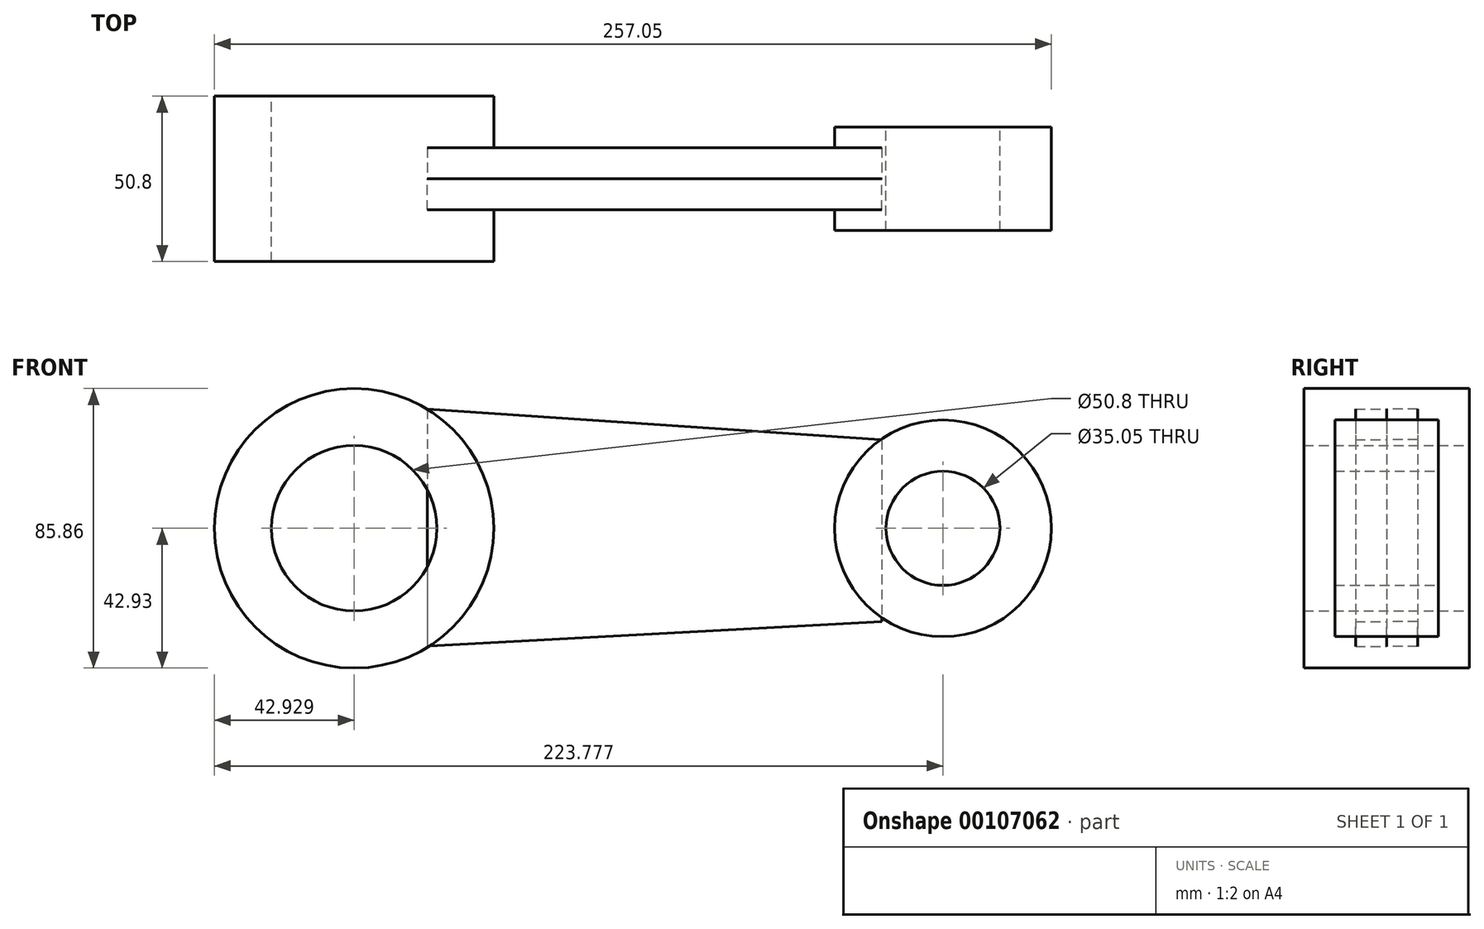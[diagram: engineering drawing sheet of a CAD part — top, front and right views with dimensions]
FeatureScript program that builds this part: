
annotation { "Feature Type Name" : "Feature", "Feature Type Description" : "" }
export const myFeature = defineFeature(function(context is Context, id is Id, definition is map)
    precondition{}
    {
        {
            var Q0;
            Q0=qCreatedBy(makeId("Front.planeOp"),FACE);
            var sketch = newSketch(context, id + "F0", { "sketchPlane" : qUnion([Q0])});
            skLineSegment(sketch, "E0", {"start": v(-64.98, 0) * mm, "end": v(115.87, 0) * mm});
            skCircle(sketch, "E1", {"center": v(-64.98, 0) * mm, "radius": 25.4 * mm});
            skCircle(sketch, "E2", {"center": v(-64.98, 0) * mm, "radius": 42.93 * mm});
            skCircle(sketch, "E3", {"center": v(115.87, 0) * mm, "radius": 17.53 * mm});
            skCircle(sketch, "E4", {"center": v(115.87, 0) * mm, "radius": 33.27 * mm});
            skSolve(sketch);
        }
        {
            var Q0;
            Q0=makeQuery(id+"F0.imprint","IMPRINT",FACE,{"disambiguationData":[TD([[makeQuery(id+"F0.imprint","IMPRINT",EDGE,{"derivedFrom":sQuery(id+"F0.wireOp",EDGE,"E3")}),-1.0]])]});
            extrude(context, id + "F1", {"entities" : qUnion([Q0]), "depth" : 15.88 * mm});
        }
        {
            var Q0;
            Q0=makeQuery(id+"F0.imprint","IMPRINT",FACE,{"disambiguationData":[TD([[makeQuery(id+"F0.imprint","IMPRINT",EDGE,{"derivedFrom":sQuery(id+"F0.wireOp",EDGE,"E1")}),-1.0]])]});
            extrude(context, id + "F2", {"entities" : qUnion([Q0]), "depth" : 25.4 * mm});
        }
        {
            var Q0;
            Q0=makeQuery(id+"F0.imprint","IMPRINT",FACE,{"disambiguationData":[TD([[makeQuery(id+"F0.imprint","IMPRINT",EDGE,{"derivedFrom":sQuery(id+"F0.wireOp",EDGE,"E1")}),-1.0]])]});
            extrude(context, id + "F3", {"entities" : qUnion([Q0]), "operationType" : NewBodyOperationType.ADD, "oppositeDirection" : true, "depth" : 25.4 * mm});
        }
        {
            var Q0;
            Q0=makeQuery(id+"F0.imprint","IMPRINT",FACE,{"disambiguationData":[TD([[makeQuery(id+"F0.imprint","IMPRINT",EDGE,{"derivedFrom":sQuery(id+"F0.wireOp",EDGE,"E3")}),-1.0]])]});
            extrude(context, id + "F4", {"entities" : qUnion([Q0]), "operationType" : NewBodyOperationType.ADD, "oppositeDirection" : true, "depth" : 15.88 * mm});
        }
        {
            var Q0;
            Q0=qCreatedBy(makeId("Front.planeOp"),FACE);
            var sketch = newSketch(context, id + "F5", { "sketchPlane" : qUnion([Q0])});
            skLineSegment(sketch, "E5", {"start": v(-42.55, 36.6) * mm, "end": v(97.09, 27.16) * mm});
            skLineSegment(sketch, "E6", {"start": v(-42.55, -36.24) * mm, "end": v(97.09, -28.65) * mm});
            skLineSegment(sketch, "E7", {"start": v(97.09, 27.16) * mm, "end": v(97.09, -28.65) * mm});
            skLineSegment(sketch, "E8", {"start": v(-42.55, 36.6) * mm, "end": v(-42.55, -36.24) * mm});
            skSolve(sketch);
        }
        {
            var Q0;
            Q0=makeQuery(id+"F5.imprint","IMPRINT",FACE,{"disambiguationData":[TD([[makeQuery(id+"F5.imprint","IMPRINT",EDGE,{"derivedFrom":sQuery(id+"F5.wireOp",EDGE,"E5")}),-1.0]])]});
            extrude(context, id + "F6", {"entities" : qUnion([Q0]), "depth" : 9.52 * mm});
        }
        {
            var Q0;
            Q0=makeQuery(id+"F6.opExtrude","CAP_FACE",FACE,{"disambiguationData":[OSD([sQuery(id+"F5.wireOp",EDGE,"E5"),sQuery(id+"F5.wireOp",EDGE,"E6"),sQuery(id+"F5.wireOp",EDGE,"E7"),sQuery(id+"F5.wireOp",EDGE,"E8")])],"isStart":true});
            extrude(context, id + "F7", {"entities" : qUnion([Q0]), "depth" : 9.52 * mm});
        }
    });
